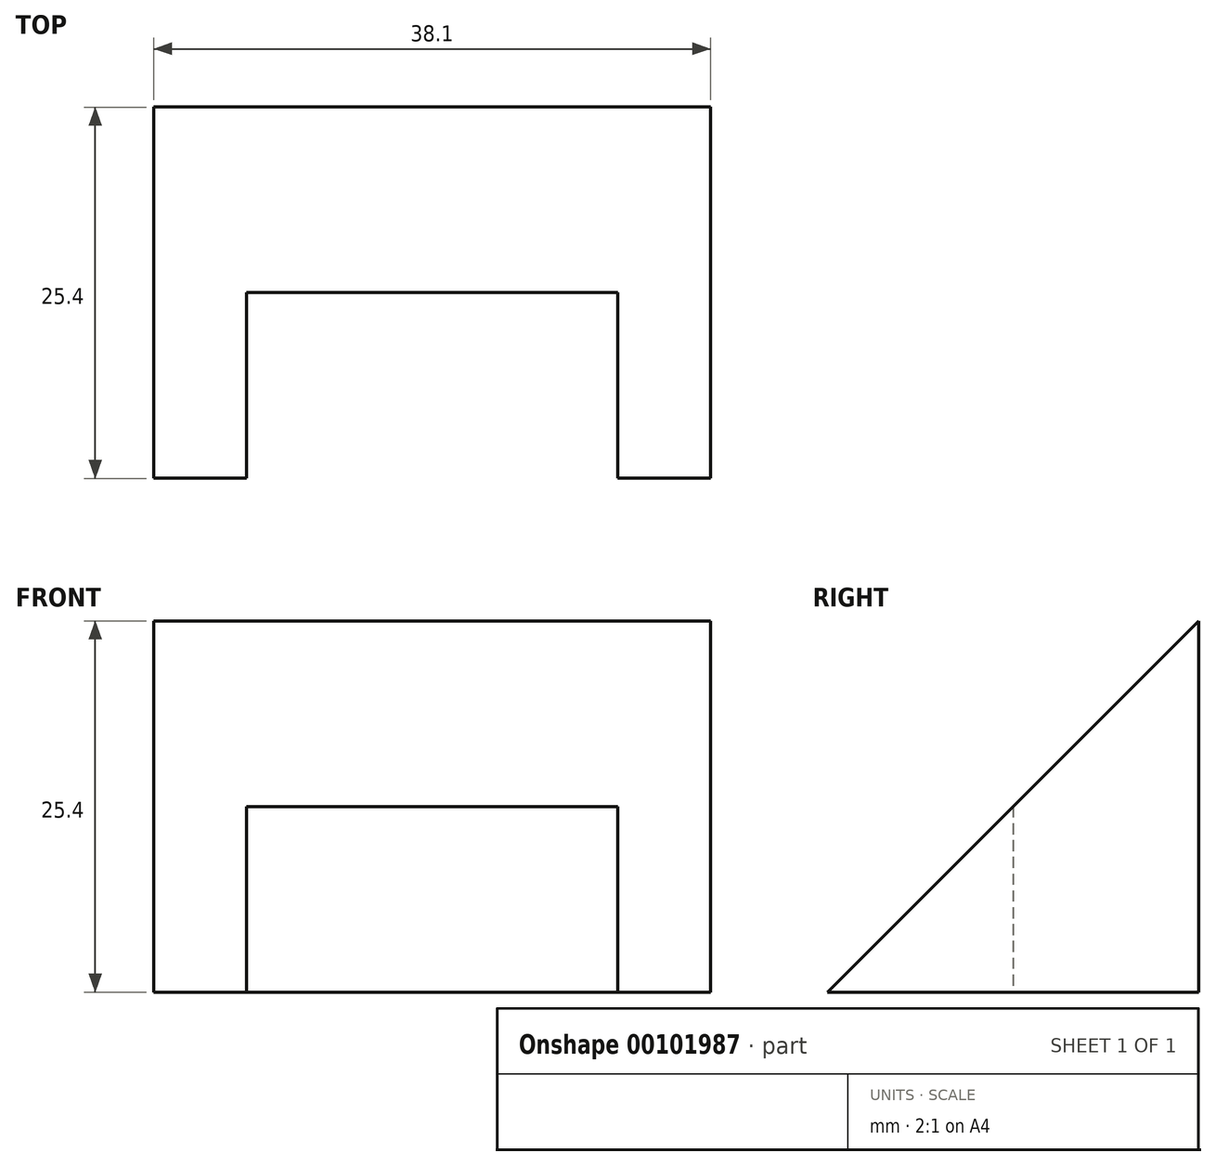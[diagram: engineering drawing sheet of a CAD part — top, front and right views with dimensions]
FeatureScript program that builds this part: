
annotation { "Feature Type Name" : "Feature", "Feature Type Description" : "" }
export const myFeature = defineFeature(function(context is Context, id is Id, definition is map)
    precondition{}
    {
        {
            var Q0;
            Q0=qCreatedBy(makeId("Right.planeOp"),FACE);
            var sketch = newSketch(context, id + "F0", { "sketchPlane" : qUnion([Q0])});
            skLineSegment(sketch, "E0", {"start": v(-6.13, -7.72) * mm, "end": v(19.27, -7.72) * mm});
            skLineSegment(sketch, "E1", {"start": v(19.27, -7.72) * mm, "end": v(19.27, 17.68) * mm});
            skLineSegment(sketch, "E2", {"start": v(19.27, 17.68) * mm, "end": v(-6.13, -7.72) * mm});
            skLineSegment(sketch, "E3", {"start": v(6.57, 4.98) * mm, "end": v(6.57, -7.72) * mm});
            skSolve(sketch);
        }
        {
            var Q0;
            {var subQ3=sQuery(id+"F0.wireOp",EDGE,"E3");Q0=makeQuery(id+"F0.imprint","IMPRINT",FACE,{"disambiguationData":[TD([[makeQuery(id+"F0.imprint","IMPRINT",EDGE,{"derivedFrom":subQ3}),-1.0]])]});}
            var Q1;
            {var subQ0=sQuery(id+"F0.wireOp",EDGE,"E1");Q1=makeQuery(id+"F0.imprint","IMPRINT",FACE,{"disambiguationData":[TD([[makeQuery(id+"F0.imprint","IMPRINT",EDGE,{"derivedFrom":subQ0}),1.0]])]});}
            extrude(context, id + "F1", {"entities" : qUnion([Q0, Q1]), "oppositeDirection" : true, "depth" : 38.1 * mm});
        }
        {
            var Q0;
            {var subQ3=sQuery(id+"F0.wireOp",EDGE,"E3");Q0=makeQuery(id+"F0.imprint","IMPRINT",FACE,{"disambiguationData":[TD([[makeQuery(id+"F0.imprint","IMPRINT",EDGE,{"derivedFrom":subQ3}),-1.0]])]});}
            extrude(context, id + "F2", {"entities" : qUnion([Q0]), "operationType" : NewBodyOperationType.REMOVE, "oppositeDirection" : true, "depth" : 31.75 * mm, "hasSecondDirection" : true, "secondDirectionOppositeDirection" : true, "secondDirectionDepth" : 6.35 * mm});
        }
    });
